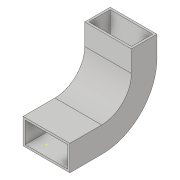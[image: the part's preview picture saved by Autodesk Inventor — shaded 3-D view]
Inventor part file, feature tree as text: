
AUTODESK INVENTOR PART (.ipt)
format: ipt  version: 2018.2 (Build 222227000, 227)  size: 102,912 bytes
history: native  units: in
note: dims shown in document units (in); Inventor stores cm internally (conversion verified against a paired STEP export)
features: sketch x3, sweep x1
ambient origin geometry x8: Origin, YZ Plane, XZ Plane, XY Plane, X Axis, Y Axis, Z Axis, Center Point
bodies: Solid1 (feature_tree)
feature tree (4):
  sketch  "Sketch1"  dims[d0=3.937in d1=1.9685in]
  sweep  "Sweep1"
  sketch  "Sketch2"  dims[d2=4.3307in]
  sketch  "Sketch3"  dims[d3=2.3622in d7=0.0in d8=0.0in]
